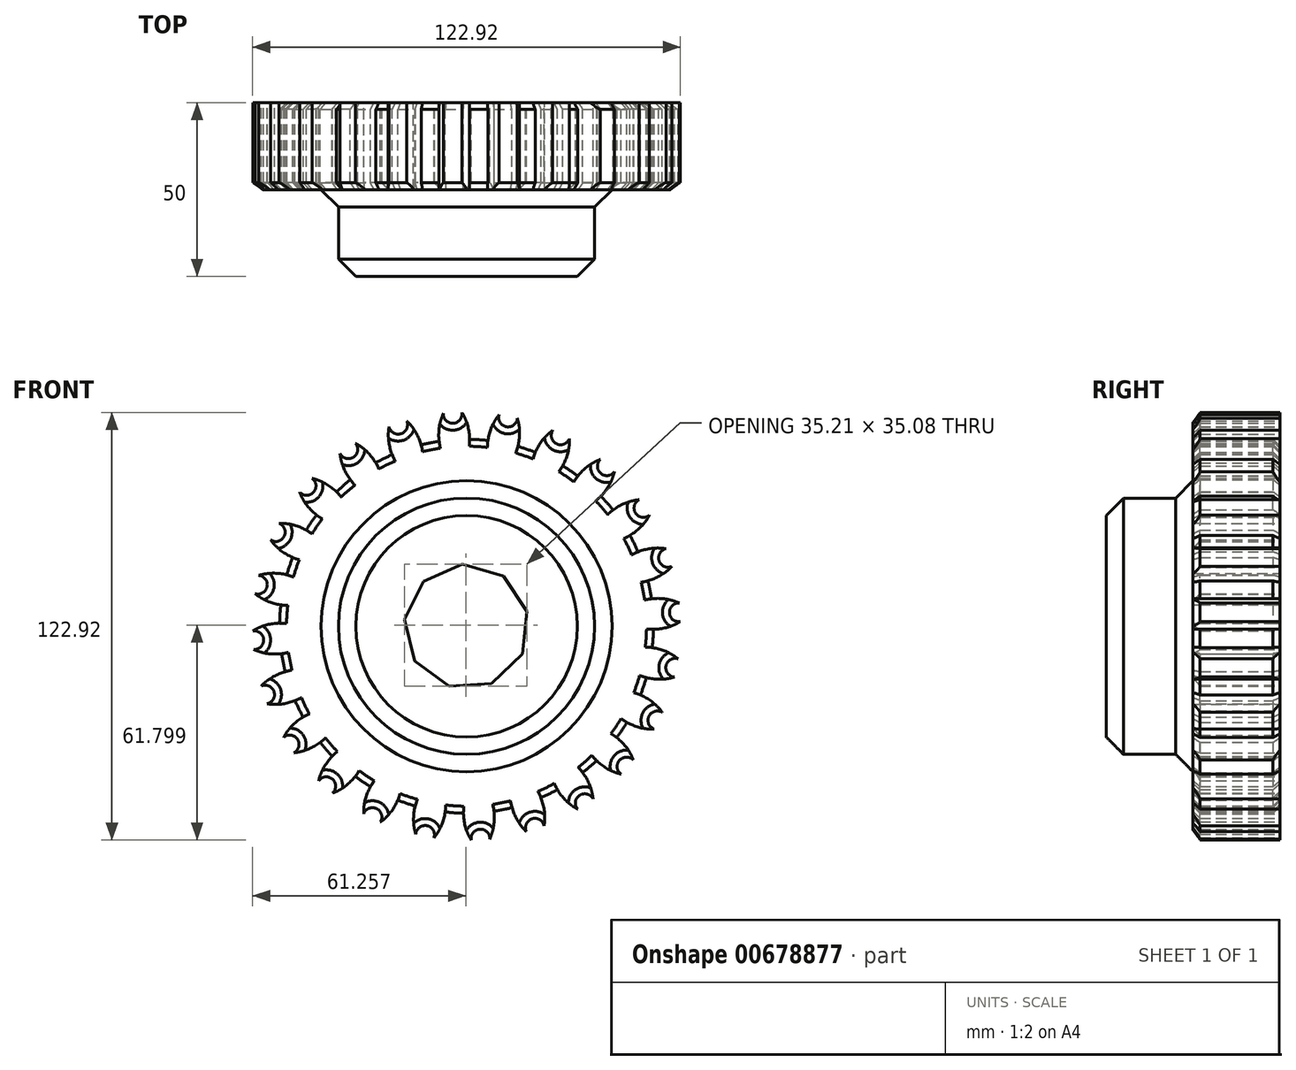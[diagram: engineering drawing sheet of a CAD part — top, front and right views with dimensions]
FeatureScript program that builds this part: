
annotation { "Feature Type Name" : "Feature", "Feature Type Description" : "" }
export const myFeature = defineFeature(function(context is Context, id is Id, definition is map)
    precondition{}
    {
        {
            var Q0;
            Q0=qCreatedBy(makeId("Front.planeOp"),FACE);
            var sketch = newSketch(context, id + "F0", { "sketchPlane" : qUnion([Q0])});
            skCircle(sketch, "E0", {"center": v(0, 0) * mm, "radius": 53.72 * mm});
            skCircle(sketch, "E1", {"center": v(0, 0) * mm, "radius": 58.67 * mm, "construction": true});
            skCircle(sketch, "E2", {"center": v(0, 0) * mm, "radius": 63.5 * mm, "construction": true});
            skLineSegment(sketch, "E3", {"start": v(0, 0) * mm, "end": v(0, 101.64) * mm, "construction": true});
            skLineSegment(sketch, "E4", {"start": v(0, 0) * mm, "end": v(-7.05, 107.5) * mm, "construction": true});
            skLineSegment(sketch, "E5", {"start": v(0, 58.67) * mm, "end": v(-85.15, 58.67) * mm, "construction": true});
            skLineSegment(sketch, "E6", {"start": v(0, 58.67) * mm, "end": v(-80.84, 29.25) * mm, "construction": true});
            skCircle(sketch, "E7", {"center": v(0, 0) * mm, "radius": 55.14 * mm, "construction": true});
            skCircle(sketch, "E8", {"center": v(0, 58.67) * mm, "radius": 14.6 * mm, "construction": true});
            skCircle(sketch, "E9", {"center": v(-13.72, 53.68) * mm, "radius": 14.6 * mm, "construction": true});
            skArc(sketch, "E10", {"start": v(0, 58.67) * mm, "mid": v(-1.19, 61.2) * mm, "end": v(-2.86, 63.44) * mm});
            skArc(sketch, "E11", {"start": v(0.88, 53.71) * mm, "mid": v(0.64, 56.23) * mm, "end": v(0, 58.67) * mm});
            skArc(sketch, "E12.MirrorCS", {"start": v(-7.66, 58.17) * mm, "mid": v(-6.81, 60.83) * mm, "end": v(-5.45, 63.27) * mm});
            skArc(sketch, "E13.MirrorCS", {"start": v(-7.88, 53.14) * mm, "mid": v(-7.98, 55.66) * mm, "end": v(-7.66, 58.17) * mm});
            skArc(sketch, "E14", {"start": v(-5.45, 63.27) * mm, "mid": v(-3.82, 58.31) * mm, "end": v(-2.86, 63.44) * mm});
            skCircle(sketch, "E15", {"center": v(0, 0) * mm, "radius": 36.8 * mm});
            skCircle(sketch, "E16.cCircle", {"center": v(0, 0) * mm, "radius": 17.92 * mm, "construction": true});
            skLineSegment(sketch, "E16.0", {"start": v(7.22, -16.4) * mm, "end": v(-5.01, -17.2) * mm});
            skLineSegment(sketch, "E16.1", {"start": v(-5.01, -17.2) * mm, "end": v(-14.9, -9.95) * mm});
            skLineSegment(sketch, "E16.2", {"start": v(-14.9, -9.95) * mm, "end": v(-17.8, 1.95) * mm});
            skLineSegment(sketch, "E16.3", {"start": v(-17.8, 1.95) * mm, "end": v(-12.39, 12.94) * mm});
            skLineSegment(sketch, "E16.4", {"start": v(-12.39, 12.94) * mm, "end": v(-1.17, 17.88) * mm});
            skLineSegment(sketch, "E16.5", {"start": v(-1.17, 17.88) * mm, "end": v(10.6, 14.45) * mm});
            skLineSegment(sketch, "E16.6", {"start": v(10.6, 14.45) * mm, "end": v(17.4, 4.26) * mm});
            skLineSegment(sketch, "E16.7", {"start": v(17.4, 4.26) * mm, "end": v(16.07, -7.92) * mm});
            skLineSegment(sketch, "E16.8", {"start": v(16.07, -7.92) * mm, "end": v(7.22, -16.4) * mm});
            skSolve(sketch);
        }
        {
            var Q0;
            {var subQ0=sQuery(id+"F0.wireOp",EDGE,"E0");var subQ1=makeQuery(id+"F0.imprint","INTERSECT",VERTEX,{"derivedFrom":[subQ0,sQuery(id+"F0.wireOp",EDGE,"E11")]});Q0=makeQuery(id+"F0.imprint","IMPRINT",FACE,{"disambiguationData":[TD([[makeQuery(id+"F0.imprint","IMPRINT",EDGE,{"disambiguationData":[TD([[subQ1,-1.0]])],"derivedFrom":subQ0}),1.0]])]});}
            var Q1;
            Q1=makeQuery(id+"F0.imprint","IMPRINT",FACE,{"disambiguationData":[TD([[makeQuery(id+"F0.imprint","IMPRINT",EDGE,{"derivedFrom":sQuery(id+"F0.wireOp",EDGE,"E10")}),1.0]])]});
            extrude(context, id + "F1", {"entities" : qUnion([Q0, Q1]), "depth" : 25 * mm, "offsetDistance" : 25 * mm});
        }
        {
            var Q0;
            Q0=makeQuery(id+"F1.opExtrude","SWEPT_BODY",BODY,{"disambiguationData":[OSD([sQuery(id+"F0.wireOp",EDGE,"E0"),sQuery(id+"F0.wireOp",EDGE,"E10"),sQuery(id+"F0.wireOp",EDGE,"E11"),sQuery(id+"F0.wireOp",EDGE,"E12.MirrorCS"),sQuery(id+"F0.wireOp",EDGE,"E13.MirrorCS"),sQuery(id+"F0.wireOp",EDGE,"E14")])]});
            var Q1;
            Q1=makeQuery(id+"F1.opExtrude","SWEPT_FACE",FACE,{"disambiguationData":[OSD([sQuery(id+"F0.wireOp",EDGE,"E0")])]});
            circularPattern(context, id + "F2", {"operationType" : NewBodyOperationType.ADD, "entities" : qUnion([Q0]), "axis" : qUnion([Q1]), "angle" : 360 * degree, "instanceCount" : 24, "equalSpace" : true});
        }
        {
            var Q0;
            Q0=makeQuery(id+"F0.imprint","IMPRINT",FACE,{"disambiguationData":[TD([[makeQuery(id+"F0.imprint","IMPRINT",EDGE,{"derivedFrom":sQuery(id+"F0.wireOp",EDGE,"E15")}),1.0]])]});
            extrude(context, id + "F3", {"entities" : qUnion([Q0]), "operationType" : NewBodyOperationType.ADD, "depth" : 50 * mm, "offsetDistance" : 25 * mm});
        }
        {
            var Q0;
            Q0=makeQuery(id+"F3.opExtrude","CAP_EDGE",EDGE,{"disambiguationData":[OSD([sQuery(id+"F0.wireOp",EDGE,"E15")])],"isStart":false});
            var Q1;
            Q1=makeQuery(id+"F3.opExtrude","SWEPT_FACE",FACE,{"disambiguationData":[OSD([sQuery(id+"F0.wireOp",EDGE,"E15")])]});
            chamfer(context, id + "F4", {"entities" : qUnion([Q0, Q1]), "width" : 5 * mm, "tangentPropagation" : true});
        }
        {
            var Q0;
            Q0=makeQuery(id+"F2.opPattern","COPY",EDGE,{"derivedFrom":makeQuery(id+"F1.opExtrude","CAP_EDGE",EDGE,{"disambiguationData":[OSD([sQuery(id+"F0.wireOp",EDGE,"E14")])],"isStart":false}),"instanceName":"20"});
            var Q1;
            Q1=makeQuery(id+"F2.opPattern","COPY",EDGE,{"derivedFrom":makeQuery(id+"F1.opExtrude","CAP_EDGE",EDGE,{"disambiguationData":[OSD([sQuery(id+"F0.wireOp",EDGE,"E14")])],"isStart":false}),"instanceName":"10"});
            var Q2;
            Q2=makeQuery(id+"F2.opPattern","COPY",EDGE,{"derivedFrom":makeQuery(id+"F1.opExtrude","CAP_EDGE",EDGE,{"disambiguationData":[OSD([sQuery(id+"F0.wireOp",EDGE,"E14")])],"isStart":true}),"instanceName":"9"});
            var Q3;
            Q3=makeQuery(id+"F2.opPattern","COPY",EDGE,{"derivedFrom":makeQuery(id+"F1.opExtrude","CAP_EDGE",EDGE,{"disambiguationData":[OSD([sQuery(id+"F0.wireOp",EDGE,"E14")])],"isStart":true}),"instanceName":"8"});
            var Q4;
            Q4=makeQuery(id+"F2.opPattern","COPY",EDGE,{"derivedFrom":makeQuery(id+"F1.opExtrude","CAP_EDGE",EDGE,{"disambiguationData":[OSD([sQuery(id+"F0.wireOp",EDGE,"E14")])],"isStart":true}),"instanceName":"7"});
            var Q5;
            Q5=makeQuery(id+"F2.opPattern","COPY",EDGE,{"derivedFrom":makeQuery(id+"F1.opExtrude","CAP_EDGE",EDGE,{"disambiguationData":[OSD([sQuery(id+"F0.wireOp",EDGE,"E14")])],"isStart":false}),"instanceName":"14"});
            var Q6;
            Q6=makeQuery(id+"F2.opPattern","COPY",EDGE,{"derivedFrom":makeQuery(id+"F1.opExtrude","CAP_EDGE",EDGE,{"disambiguationData":[OSD([sQuery(id+"F0.wireOp",EDGE,"E14")])],"isStart":false}),"instanceName":"11"});
            var Q7;
            Q7=makeQuery(id+"F2.opPattern","COPY",EDGE,{"derivedFrom":makeQuery(id+"F1.opExtrude","CAP_EDGE",EDGE,{"disambiguationData":[OSD([sQuery(id+"F0.wireOp",EDGE,"E14")])],"isStart":false}),"instanceName":"9"});
            var Q8;
            Q8=makeQuery(id+"F2.opPattern","COPY",EDGE,{"derivedFrom":makeQuery(id+"F1.opExtrude","CAP_EDGE",EDGE,{"disambiguationData":[OSD([sQuery(id+"F0.wireOp",EDGE,"E14")])],"isStart":false}),"instanceName":"8"});
            var Q9;
            Q9=makeQuery(id+"F2.opPattern","COPY",EDGE,{"derivedFrom":makeQuery(id+"F1.opExtrude","CAP_EDGE",EDGE,{"disambiguationData":[OSD([sQuery(id+"F0.wireOp",EDGE,"E14")])],"isStart":false}),"instanceName":"7"});
            var Q10;
            {var subQ1=sQuery(id+"F0.wireOp",EDGE,"E11");var subQ2=sQuery(id+"F0.wireOp",EDGE,"E0");Q10=makeQuery(id+"F3.boolean.opBoolean","SPLIT",EDGE,{"disambiguationData":[TD([makeQuery(id+"F2.opPattern","COPY",FACE,{"derivedFrom":makeQuery(id+"F1.opExtrude","SWEPT_FACE",FACE,{"disambiguationData":[OSD([subQ1])]}),"instanceName":"13"})])],"derivedFrom":makeQuery(id+"F1.opExtrude","CAP_EDGE",EDGE,{"disambiguationData":[OSD([subQ2])],"isStart":false})});}
            var Q11;
            {var subQ2=sQuery(id+"F0.wireOp",EDGE,"E11");var subQ3=sQuery(id+"F0.wireOp",EDGE,"E0");Q11=makeQuery(id+"F3.boolean.opBoolean","SPLIT",EDGE,{"disambiguationData":[TD([makeQuery(id+"F2.opPattern","COPY",FACE,{"derivedFrom":makeQuery(id+"F1.opExtrude","SWEPT_FACE",FACE,{"disambiguationData":[OSD([subQ2])]}),"instanceName":"14"})])],"derivedFrom":makeQuery(id+"F1.opExtrude","CAP_EDGE",EDGE,{"disambiguationData":[OSD([subQ3])],"isStart":true})});}
            var Q12;
            {var subQ1=sQuery(id+"F0.wireOp",EDGE,"E11");var subQ2=sQuery(id+"F0.wireOp",EDGE,"E0");Q12=makeQuery(id+"F3.boolean.opBoolean","SPLIT",EDGE,{"disambiguationData":[TD([makeQuery(id+"F2.opPattern","COPY",FACE,{"derivedFrom":makeQuery(id+"F1.opExtrude","SWEPT_FACE",FACE,{"disambiguationData":[OSD([subQ1])]}),"instanceName":"15"})])],"derivedFrom":makeQuery(id+"F1.opExtrude","CAP_EDGE",EDGE,{"disambiguationData":[OSD([subQ2])],"isStart":false})});}
            var Q13;
            {var subQ1=sQuery(id+"F0.wireOp",EDGE,"E11");var subQ2=sQuery(id+"F0.wireOp",EDGE,"E0");Q13=makeQuery(id+"F3.boolean.opBoolean","SPLIT",EDGE,{"disambiguationData":[TD([makeQuery(id+"F2.opPattern","COPY",FACE,{"derivedFrom":makeQuery(id+"F1.opExtrude","SWEPT_FACE",FACE,{"disambiguationData":[OSD([subQ1])]}),"instanceName":"18"})])],"derivedFrom":makeQuery(id+"F1.opExtrude","CAP_EDGE",EDGE,{"disambiguationData":[OSD([subQ2])],"isStart":false})});}
            var Q14;
            {var subQ1=sQuery(id+"F0.wireOp",EDGE,"E11");var subQ2=sQuery(id+"F0.wireOp",EDGE,"E0");Q14=makeQuery(id+"F3.boolean.opBoolean","SPLIT",EDGE,{"disambiguationData":[TD([makeQuery(id+"F2.opPattern","COPY",FACE,{"derivedFrom":makeQuery(id+"F1.opExtrude","SWEPT_FACE",FACE,{"disambiguationData":[OSD([subQ1])]}),"instanceName":"19"})])],"derivedFrom":makeQuery(id+"F1.opExtrude","CAP_EDGE",EDGE,{"disambiguationData":[OSD([subQ2])],"isStart":false})});}
            var Q15;
            {var subQ1=sQuery(id+"F0.wireOp",EDGE,"E11");var subQ2=sQuery(id+"F0.wireOp",EDGE,"E0");Q15=makeQuery(id+"F3.boolean.opBoolean","SPLIT",EDGE,{"disambiguationData":[TD([makeQuery(id+"F2.opPattern","COPY",FACE,{"derivedFrom":makeQuery(id+"F1.opExtrude","SWEPT_FACE",FACE,{"disambiguationData":[OSD([subQ1])]}),"instanceName":"20"})])],"derivedFrom":makeQuery(id+"F1.opExtrude","CAP_EDGE",EDGE,{"disambiguationData":[OSD([subQ2])],"isStart":false})});}
            var Q16;
            Q16=makeQuery(id+"F2.opPattern","COPY",EDGE,{"derivedFrom":makeQuery(id+"F1.opExtrude","CAP_EDGE",EDGE,{"disambiguationData":[OSD([sQuery(id+"F0.wireOp",EDGE,"E14")])],"isStart":false}),"instanceName":"22"});
            var Q17;
            Q17=makeQuery(id+"F2.opPattern","COPY",EDGE,{"derivedFrom":makeQuery(id+"F1.opExtrude","CAP_EDGE",EDGE,{"disambiguationData":[OSD([sQuery(id+"F0.wireOp",EDGE,"E14")])],"isStart":false}),"instanceName":"23"});
            var Q18;
            Q18=makeQuery(id+"F1.opExtrude","CAP_EDGE",EDGE,{"disambiguationData":[OSD([sQuery(id+"F0.wireOp",EDGE,"E14")])],"isStart":false});
            var Q19;
            Q19=makeQuery(id+"F2.opPattern","COPY",EDGE,{"derivedFrom":makeQuery(id+"F1.opExtrude","CAP_EDGE",EDGE,{"disambiguationData":[OSD([sQuery(id+"F0.wireOp",EDGE,"E14")])],"isStart":false}),"instanceName":"13"});
            var Q20;
            Q20=makeQuery(id+"F2.opPattern","COPY",EDGE,{"derivedFrom":makeQuery(id+"F1.opExtrude","CAP_EDGE",EDGE,{"disambiguationData":[OSD([sQuery(id+"F0.wireOp",EDGE,"E14")])],"isStart":false}),"instanceName":"12"});
            var Q21;
            {var subQ1=sQuery(id+"F0.wireOp",EDGE,"E11");var subQ2=sQuery(id+"F0.wireOp",EDGE,"E0");Q21=makeQuery(id+"F3.boolean.opBoolean","SPLIT",EDGE,{"disambiguationData":[TD([makeQuery(id+"F2.opPattern","COPY",FACE,{"derivedFrom":makeQuery(id+"F1.opExtrude","SWEPT_FACE",FACE,{"disambiguationData":[OSD([subQ1])]}),"instanceName":"12"})])],"derivedFrom":makeQuery(id+"F1.opExtrude","CAP_EDGE",EDGE,{"disambiguationData":[OSD([subQ2])],"isStart":false})});}
            var Q22;
            {var subQ1=sQuery(id+"F0.wireOp",EDGE,"E11");var subQ2=sQuery(id+"F0.wireOp",EDGE,"E0");Q22=makeQuery(id+"F3.boolean.opBoolean","SPLIT",EDGE,{"disambiguationData":[TD([makeQuery(id+"F2.opPattern","COPY",FACE,{"derivedFrom":makeQuery(id+"F1.opExtrude","SWEPT_FACE",FACE,{"disambiguationData":[OSD([subQ1])]}),"instanceName":"11"})])],"derivedFrom":makeQuery(id+"F1.opExtrude","CAP_EDGE",EDGE,{"disambiguationData":[OSD([subQ2])],"isStart":false})});}
            var Q23;
            {var subQ1=sQuery(id+"F0.wireOp",EDGE,"E11");var subQ2=sQuery(id+"F0.wireOp",EDGE,"E0");Q23=makeQuery(id+"F3.boolean.opBoolean","SPLIT",EDGE,{"disambiguationData":[TD([makeQuery(id+"F2.opPattern","COPY",FACE,{"derivedFrom":makeQuery(id+"F1.opExtrude","SWEPT_FACE",FACE,{"disambiguationData":[OSD([subQ1])]}),"instanceName":"10"})])],"derivedFrom":makeQuery(id+"F1.opExtrude","CAP_EDGE",EDGE,{"disambiguationData":[OSD([subQ2])],"isStart":false})});}
            var Q24;
            {var subQ1=sQuery(id+"F0.wireOp",EDGE,"E11");var subQ2=sQuery(id+"F0.wireOp",EDGE,"E0");Q24=makeQuery(id+"F3.boolean.opBoolean","SPLIT",EDGE,{"disambiguationData":[TD([makeQuery(id+"F2.opPattern","COPY",FACE,{"derivedFrom":makeQuery(id+"F1.opExtrude","SWEPT_FACE",FACE,{"disambiguationData":[OSD([subQ1])]}),"instanceName":"9"})])],"derivedFrom":makeQuery(id+"F1.opExtrude","CAP_EDGE",EDGE,{"disambiguationData":[OSD([subQ2])],"isStart":false})});}
            var Q25;
            {var subQ1=sQuery(id+"F0.wireOp",EDGE,"E11");var subQ2=sQuery(id+"F0.wireOp",EDGE,"E0");Q25=makeQuery(id+"F3.boolean.opBoolean","SPLIT",EDGE,{"disambiguationData":[TD([makeQuery(id+"F2.opPattern","COPY",FACE,{"derivedFrom":makeQuery(id+"F1.opExtrude","SWEPT_FACE",FACE,{"disambiguationData":[OSD([subQ1])]}),"instanceName":"8"})])],"derivedFrom":makeQuery(id+"F1.opExtrude","CAP_EDGE",EDGE,{"disambiguationData":[OSD([subQ2])],"isStart":false})});}
            var Q26;
            {var subQ1=sQuery(id+"F0.wireOp",EDGE,"E11");var subQ2=sQuery(id+"F0.wireOp",EDGE,"E0");Q26=makeQuery(id+"F3.boolean.opBoolean","SPLIT",EDGE,{"disambiguationData":[TD([makeQuery(id+"F2.opPattern","COPY",FACE,{"derivedFrom":makeQuery(id+"F1.opExtrude","SWEPT_FACE",FACE,{"disambiguationData":[OSD([subQ1])]}),"instanceName":"7"})])],"derivedFrom":makeQuery(id+"F1.opExtrude","CAP_EDGE",EDGE,{"disambiguationData":[OSD([subQ2])],"isStart":false})});}
            var Q27;
            {var subQ1=sQuery(id+"F0.wireOp",EDGE,"E11");var subQ2=sQuery(id+"F0.wireOp",EDGE,"E0");Q27=makeQuery(id+"F3.boolean.opBoolean","SPLIT",EDGE,{"disambiguationData":[TD([makeQuery(id+"F2.opPattern","COPY",FACE,{"derivedFrom":makeQuery(id+"F1.opExtrude","SWEPT_FACE",FACE,{"disambiguationData":[OSD([subQ1])]}),"instanceName":"6"})])],"derivedFrom":makeQuery(id+"F1.opExtrude","CAP_EDGE",EDGE,{"disambiguationData":[OSD([subQ2])],"isStart":false})});}
            var Q28;
            Q28=makeQuery(id+"F2.opPattern","COPY",EDGE,{"derivedFrom":makeQuery(id+"F1.opExtrude","CAP_EDGE",EDGE,{"disambiguationData":[OSD([sQuery(id+"F0.wireOp",EDGE,"E14")])],"isStart":false}),"instanceName":"6"});
            var Q29;
            Q29=makeQuery(id+"F2.opPattern","COPY",EDGE,{"derivedFrom":makeQuery(id+"F1.opExtrude","CAP_EDGE",EDGE,{"disambiguationData":[OSD([sQuery(id+"F0.wireOp",EDGE,"E14")])],"isStart":false}),"instanceName":"5"});
            var Q30;
            {var subQ1=sQuery(id+"F0.wireOp",EDGE,"E11");var subQ2=sQuery(id+"F0.wireOp",EDGE,"E0");Q30=makeQuery(id+"F3.boolean.opBoolean","SPLIT",EDGE,{"disambiguationData":[TD([makeQuery(id+"F2.opPattern","COPY",FACE,{"derivedFrom":makeQuery(id+"F1.opExtrude","SWEPT_FACE",FACE,{"disambiguationData":[OSD([subQ1])]}),"instanceName":"4"})])],"derivedFrom":makeQuery(id+"F1.opExtrude","CAP_EDGE",EDGE,{"disambiguationData":[OSD([subQ2])],"isStart":false})});}
            var Q31;
            {var subQ1=sQuery(id+"F0.wireOp",EDGE,"E11");var subQ2=sQuery(id+"F0.wireOp",EDGE,"E0");Q31=makeQuery(id+"F3.boolean.opBoolean","SPLIT",EDGE,{"disambiguationData":[TD([makeQuery(id+"F2.opPattern","COPY",FACE,{"derivedFrom":makeQuery(id+"F1.opExtrude","SWEPT_FACE",FACE,{"disambiguationData":[OSD([subQ1])]}),"instanceName":"5"})])],"derivedFrom":makeQuery(id+"F1.opExtrude","CAP_EDGE",EDGE,{"disambiguationData":[OSD([subQ2])],"isStart":false})});}
            var Q32;
            Q32=makeQuery(id+"F2.opPattern","COPY",EDGE,{"derivedFrom":makeQuery(id+"F1.opExtrude","CAP_EDGE",EDGE,{"disambiguationData":[OSD([sQuery(id+"F0.wireOp",EDGE,"E14")])],"isStart":false}),"instanceName":"21"});
            var Q33;
            {var subQ1=sQuery(id+"F0.wireOp",EDGE,"E11");var subQ2=sQuery(id+"F0.wireOp",EDGE,"E0");Q33=makeQuery(id+"F3.boolean.opBoolean","SPLIT",EDGE,{"disambiguationData":[TD([makeQuery(id+"F2.opPattern","COPY",FACE,{"derivedFrom":makeQuery(id+"F1.opExtrude","SWEPT_FACE",FACE,{"disambiguationData":[OSD([subQ1])]}),"instanceName":"21"})])],"derivedFrom":makeQuery(id+"F1.opExtrude","CAP_EDGE",EDGE,{"disambiguationData":[OSD([subQ2])],"isStart":false})});}
            var Q34;
            {var subQ1=sQuery(id+"F0.wireOp",EDGE,"E11");var subQ2=sQuery(id+"F0.wireOp",EDGE,"E0");Q34=makeQuery(id+"F3.boolean.opBoolean","SPLIT",EDGE,{"disambiguationData":[TD([makeQuery(id+"F2.opPattern","COPY",FACE,{"derivedFrom":makeQuery(id+"F1.opExtrude","SWEPT_FACE",FACE,{"disambiguationData":[OSD([subQ1])]}),"instanceName":"22"})])],"derivedFrom":makeQuery(id+"F1.opExtrude","CAP_EDGE",EDGE,{"disambiguationData":[OSD([subQ2])],"isStart":false})});}
            var Q35;
            Q35=makeQuery(id+"F2.opPattern","COPY",EDGE,{"derivedFrom":makeQuery(id+"F1.opExtrude","CAP_EDGE",EDGE,{"disambiguationData":[OSD([sQuery(id+"F0.wireOp",EDGE,"E14")])],"isStart":false}),"instanceName":"18"});
            var Q36;
            Q36=makeQuery(id+"F2.opPattern","COPY",EDGE,{"derivedFrom":makeQuery(id+"F1.opExtrude","CAP_EDGE",EDGE,{"disambiguationData":[OSD([sQuery(id+"F0.wireOp",EDGE,"E14")])],"isStart":false}),"instanceName":"17"});
            var Q37;
            Q37=makeQuery(id+"F2.opPattern","COPY",EDGE,{"derivedFrom":makeQuery(id+"F1.opExtrude","CAP_EDGE",EDGE,{"disambiguationData":[OSD([sQuery(id+"F0.wireOp",EDGE,"E14")])],"isStart":false}),"instanceName":"16"});
            var Q38;
            {var subQ1=sQuery(id+"F0.wireOp",EDGE,"E11");var subQ2=sQuery(id+"F0.wireOp",EDGE,"E0");Q38=makeQuery(id+"F3.boolean.opBoolean","SPLIT",EDGE,{"disambiguationData":[TD([makeQuery(id+"F2.opPattern","COPY",FACE,{"derivedFrom":makeQuery(id+"F1.opExtrude","SWEPT_FACE",FACE,{"disambiguationData":[OSD([subQ1])]}),"instanceName":"16"})])],"derivedFrom":makeQuery(id+"F1.opExtrude","CAP_EDGE",EDGE,{"disambiguationData":[OSD([subQ2])],"isStart":false})});}
            var Q39;
            {var subQ1=sQuery(id+"F0.wireOp",EDGE,"E11");var subQ2=sQuery(id+"F0.wireOp",EDGE,"E0");Q39=makeQuery(id+"F3.boolean.opBoolean","SPLIT",EDGE,{"disambiguationData":[TD([makeQuery(id+"F2.opPattern","COPY",FACE,{"derivedFrom":makeQuery(id+"F1.opExtrude","SWEPT_FACE",FACE,{"disambiguationData":[OSD([subQ1])]}),"instanceName":"17"})])],"derivedFrom":makeQuery(id+"F1.opExtrude","CAP_EDGE",EDGE,{"disambiguationData":[OSD([subQ2])],"isStart":false})});}
            var Q40;
            {var subQ0=sQuery(id+"F0.wireOp",EDGE,"E13.MirrorCS");var subQ2=sQuery(id+"F0.wireOp",EDGE,"E0");Q40=makeQuery(id+"F3.boolean.opBoolean","SPLIT",EDGE,{"disambiguationData":[TD([makeQuery(id+"F1.opExtrude","SWEPT_FACE",FACE,{"disambiguationData":[OSD([subQ0])]})])],"derivedFrom":makeQuery(id+"F1.opExtrude","CAP_EDGE",EDGE,{"disambiguationData":[OSD([subQ2])],"isStart":false})});}
            var Q41;
            {var subQ1=sQuery(id+"F0.wireOp",EDGE,"E11");var subQ2=sQuery(id+"F0.wireOp",EDGE,"E0");Q41=makeQuery(id+"F3.boolean.opBoolean","SPLIT",EDGE,{"disambiguationData":[TD([makeQuery(id+"F1.opExtrude","SWEPT_FACE",FACE,{"disambiguationData":[OSD([subQ1])]})])],"derivedFrom":makeQuery(id+"F1.opExtrude","CAP_EDGE",EDGE,{"disambiguationData":[OSD([subQ2])],"isStart":false})});}
            var Q42;
            {var subQ1=sQuery(id+"F0.wireOp",EDGE,"E11");var subQ2=sQuery(id+"F0.wireOp",EDGE,"E0");Q42=makeQuery(id+"F3.boolean.opBoolean","SPLIT",EDGE,{"disambiguationData":[TD([makeQuery(id+"F2.opPattern","COPY",FACE,{"derivedFrom":makeQuery(id+"F1.opExtrude","SWEPT_FACE",FACE,{"disambiguationData":[OSD([subQ1])]}),"instanceName":"1"})])],"derivedFrom":makeQuery(id+"F1.opExtrude","CAP_EDGE",EDGE,{"disambiguationData":[OSD([subQ2])],"isStart":false})});}
            var Q43;
            {var subQ1=sQuery(id+"F0.wireOp",EDGE,"E11");var subQ2=sQuery(id+"F0.wireOp",EDGE,"E0");Q43=makeQuery(id+"F3.boolean.opBoolean","SPLIT",EDGE,{"disambiguationData":[TD([makeQuery(id+"F2.opPattern","COPY",FACE,{"derivedFrom":makeQuery(id+"F1.opExtrude","SWEPT_FACE",FACE,{"disambiguationData":[OSD([subQ1])]}),"instanceName":"2"})])],"derivedFrom":makeQuery(id+"F1.opExtrude","CAP_EDGE",EDGE,{"disambiguationData":[OSD([subQ2])],"isStart":false})});}
            var Q44;
            Q44=makeQuery(id+"F2.opPattern","COPY",EDGE,{"derivedFrom":makeQuery(id+"F1.opExtrude","CAP_EDGE",EDGE,{"disambiguationData":[OSD([sQuery(id+"F0.wireOp",EDGE,"E14")])],"isStart":false}),"instanceName":"1"});
            var Q45;
            Q45=makeQuery(id+"F2.opPattern","COPY",EDGE,{"derivedFrom":makeQuery(id+"F1.opExtrude","CAP_EDGE",EDGE,{"disambiguationData":[OSD([sQuery(id+"F0.wireOp",EDGE,"E14")])],"isStart":false}),"instanceName":"2"});
            var Q46;
            Q46=makeQuery(id+"F2.opPattern","COPY",EDGE,{"derivedFrom":makeQuery(id+"F1.opExtrude","CAP_EDGE",EDGE,{"disambiguationData":[OSD([sQuery(id+"F0.wireOp",EDGE,"E14")])],"isStart":true}),"instanceName":"3"});
            var Q47;
            Q47=makeQuery(id+"F2.opPattern","COPY",EDGE,{"derivedFrom":makeQuery(id+"F1.opExtrude","CAP_EDGE",EDGE,{"disambiguationData":[OSD([sQuery(id+"F0.wireOp",EDGE,"E14")])],"isStart":false}),"instanceName":"15"});
            var Q48;
            {var subQ1=sQuery(id+"F0.wireOp",EDGE,"E11");var subQ2=sQuery(id+"F0.wireOp",EDGE,"E0");Q48=makeQuery(id+"F3.boolean.opBoolean","SPLIT",EDGE,{"disambiguationData":[TD([makeQuery(id+"F2.opPattern","COPY",FACE,{"derivedFrom":makeQuery(id+"F1.opExtrude","SWEPT_FACE",FACE,{"disambiguationData":[OSD([subQ1])]}),"instanceName":"3"})])],"derivedFrom":makeQuery(id+"F1.opExtrude","CAP_EDGE",EDGE,{"disambiguationData":[OSD([subQ2])],"isStart":false})});}
            var Q49;
            Q49=makeQuery(id+"F2.opPattern","COPY",EDGE,{"derivedFrom":makeQuery(id+"F1.opExtrude","CAP_EDGE",EDGE,{"disambiguationData":[OSD([sQuery(id+"F0.wireOp",EDGE,"E14")])],"isStart":false}),"instanceName":"4"});
            var Q50;
            Q50=makeQuery(id+"F2.opPattern","COPY",EDGE,{"derivedFrom":makeQuery(id+"F1.opExtrude","CAP_EDGE",EDGE,{"disambiguationData":[OSD([sQuery(id+"F0.wireOp",EDGE,"E14")])],"isStart":false}),"instanceName":"19"});
            var Q51;
            Q51=makeQuery(id+"F2.opPattern","COPY",EDGE,{"derivedFrom":makeQuery(id+"F1.opExtrude","CAP_EDGE",EDGE,{"disambiguationData":[OSD([sQuery(id+"F0.wireOp",EDGE,"E14")])],"isStart":false}),"instanceName":"3"});
            chamfer(context, id + "F5", {"entities" : qUnion([Q0, Q1, Q2, Q3, Q4, Q5, Q6, Q7, Q8, Q9, Q10, Q11, Q12, Q13, Q14, Q15, Q16, Q17, Q18, Q19, Q20, Q21, Q22, Q23, Q24, Q25, Q26, Q27, Q28, Q29, Q30, Q31, Q32, Q33, Q34, Q35, Q36, Q37, Q38, Q39, Q40, Q41, Q42, Q43, Q44, Q45, Q46, Q47, Q48, Q49, Q50, Q51]), "width" : 2 * mm, "tangentPropagation" : true});
        }
    });
